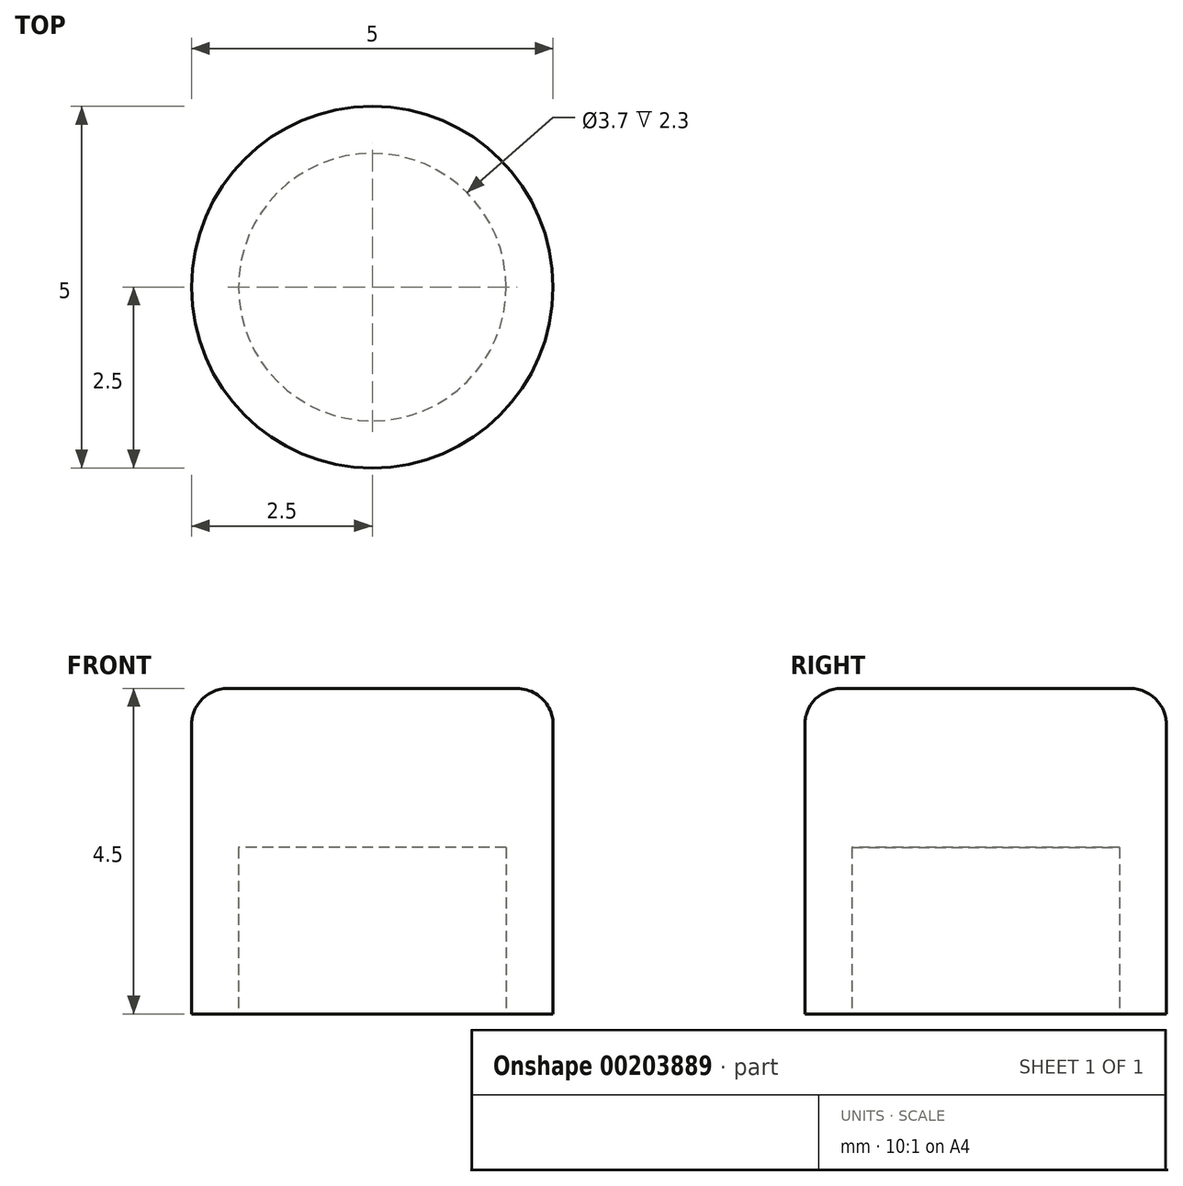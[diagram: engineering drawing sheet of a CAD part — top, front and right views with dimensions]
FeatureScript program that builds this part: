
annotation { "Feature Type Name" : "Feature", "Feature Type Description" : "" }
export const myFeature = defineFeature(function(context is Context, id is Id, definition is map)
    precondition{}
    {
        {
            var Q0;
            Q0=qCreatedBy(makeId("Top.planeOp"),FACE);
            var sketch = newSketch(context, id + "F0", { "sketchPlane" : qUnion([Q0])});
            skCircle(sketch, "E0", {"center": v(0, 0) * mm, "radius": 1.85 * mm});
            skCircle(sketch, "E1", {"center": v(0, 0) * mm, "radius": 2.5 * mm});
            skSolve(sketch);
        }
        {
            var Q0;
            Q0=makeQuery(id+"F0.imprint","IMPRINT",FACE,{"disambiguationData":[TD([[makeQuery(id+"F0.imprint","IMPRINT",EDGE,{"derivedFrom":sQuery(id+"F0.wireOp",EDGE,"E0")}),1.0]])]});
            var Q1;
            Q1=makeQuery(id+"F0.imprint","IMPRINT",FACE,{"disambiguationData":[TD([[makeQuery(id+"F0.imprint","IMPRINT",EDGE,{"derivedFrom":sQuery(id+"F0.wireOp",EDGE,"E0")}),-1.0]])]});
            extrude(context, id + "F1", {"entities" : qUnion([Q0, Q1]), "depth" : 4.5 * mm});
        }
        {
            var Q0;
            Q0=makeQuery(id+"F1.opExtrude","CAP_EDGE",EDGE,{"disambiguationData":[OSD([sQuery(id+"F0.wireOp",EDGE,"E1")])],"isStart":false});
            fillet(context, id + "F2", {"entities" : qUnion([Q0]), "radius" : .5 * mm, "tangentPropagation" : true, "allowEdgeOverflow" : false});
        }
        {
            var Q0;
            Q0=makeQuery(id+"F0.imprint","IMPRINT",FACE,{"disambiguationData":[TD([[makeQuery(id+"F0.imprint","IMPRINT",EDGE,{"derivedFrom":sQuery(id+"F0.wireOp",EDGE,"E0")}),1.0]])]});
            extrude(context, id + "F3", {"entities" : qUnion([Q0]), "operationType" : NewBodyOperationType.REMOVE, "depth" : 2.3 * mm});
        }
    });
